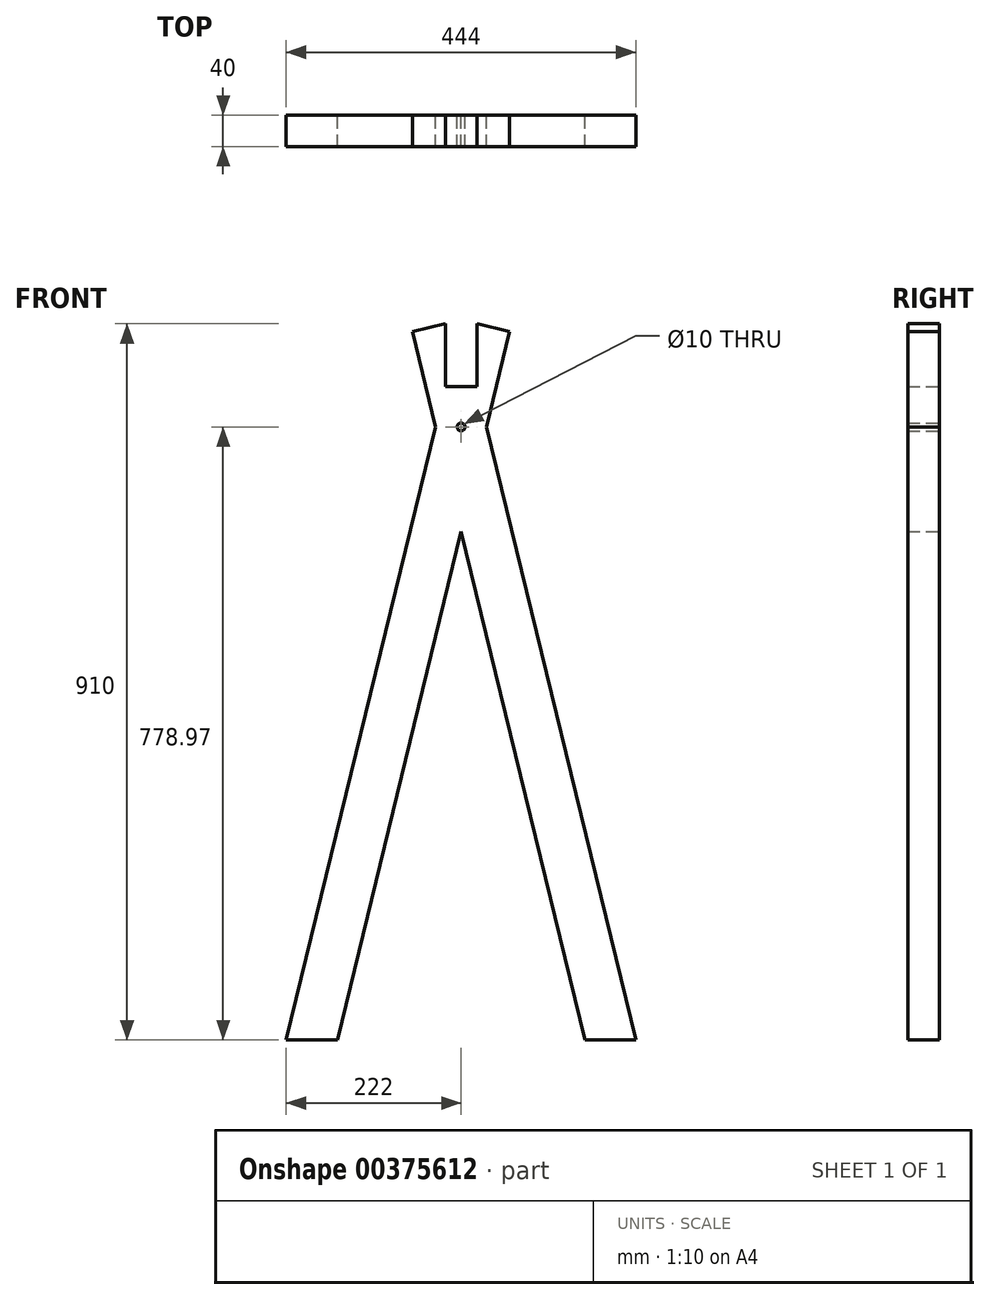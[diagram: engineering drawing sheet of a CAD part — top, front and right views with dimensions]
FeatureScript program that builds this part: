
annotation { "Feature Type Name" : "Feature", "Feature Type Description" : "" }
export const myFeature = defineFeature(function(context is Context, id is Id, definition is map)
    precondition{}
    {
        {
            var Q0;
            Q0=qCreatedBy(makeId("Front.planeOp"),FACE);
            var sketch = newSketch(context, id + "F0", { "sketchPlane" : qUnion([Q0])});
            skLineSegment(sketch, "E0.bottom", {"start": v(20, -40) * mm, "end": v(-20, -40) * mm, "construction": true});
            skLineSegment(sketch, "E0.top", {"start": v(20, 40) * mm, "end": v(-20, 40) * mm, "construction": true});
            skLineSegment(sketch, "E0.left", {"start": v(20, -40) * mm, "end": v(20, 40) * mm, "construction": true});
            skLineSegment(sketch, "E0.right", {"start": v(-20, -40) * mm, "end": v(-20, 40) * mm, "construction": true});
            skSolve(sketch);
        }
        {
            var Q0;
            Q0=qCreatedBy(makeId("Front.planeOp"),FACE);
            var sketch = newSketch(context, id + "F1", { "sketchPlane" : qUnion([Q0])});
            skLineSegment(sketch, "E1", {"start": v(-157.16, -870) * mm, "end": v(157.16, -870) * mm, "construction": true});
            skPoint(sketch, "E2", {"position": v(0, -870) * mm});
            skLineSegment(sketch, "E3.top", {"start": v(-61.83, 29.82) * mm, "end": v(157.16, -870) * mm});
            skLineSegment(sketch, "E4.bottom", {"start": v(-222, -870) * mm, "end": v(-20, -40) * mm});
            skLineSegment(sketch, "E4.top", {"start": v(-157.16, -870) * mm, "end": v(61.83, 29.82) * mm});
            skLineSegment(sketch, "E5", {"start": v(157.16, -870) * mm, "end": v(222, -870) * mm});
            skLineSegment(sketch, "E6", {"start": v(-157.16, -870) * mm, "end": v(-222, -870) * mm});
            skPoint(sketch, "E7", {"position": v(-32.42, -91.03) * mm});
            skPoint(sketch, "E8", {"position": v(32.42, -91.03) * mm});
            skLineSegment(sketch, "E9", {"start": v(-32.42, -91.03) * mm, "end": v(32.42, -91.03) * mm, "construction": true});
            skCircle(sketch, "E10", {"center": v(0, -91.03) * mm, "radius": 5 * mm});
            skPoint(sketch, "E11.middle", {"position": v(0, 0) * mm});
            skLineSegment(sketch, "E12.trimOffspring", {"start": v(20, -40) * mm, "end": v(222, -870) * mm});
            skLineSegment(sketch, "E13.0", {"start": v(20, -40) * mm, "end": v(20, 40) * mm});
            skLineSegment(sketch, "E13.2", {"start": v(-20, -40) * mm, "end": v(-20, 40) * mm});
            skLineSegment(sketch, "E13.3", {"start": v(20, -40) * mm, "end": v(-20, -40) * mm});
            skLineSegment(sketch, "E14", {"start": v(61.83, 29.82) * mm, "end": v(20, 40) * mm});
            skLineSegment(sketch, "E15", {"start": v(-61.83, 29.82) * mm, "end": v(-20, 40) * mm});
            skSolve(sketch);
        }
        {
            var Q0;
            Q0=qSketchRegion(id+"F1",true);
            extrude(context, id + "F2", {"entities" : qUnion([Q0]), "depth" : 40 * mm});
        }
    });
